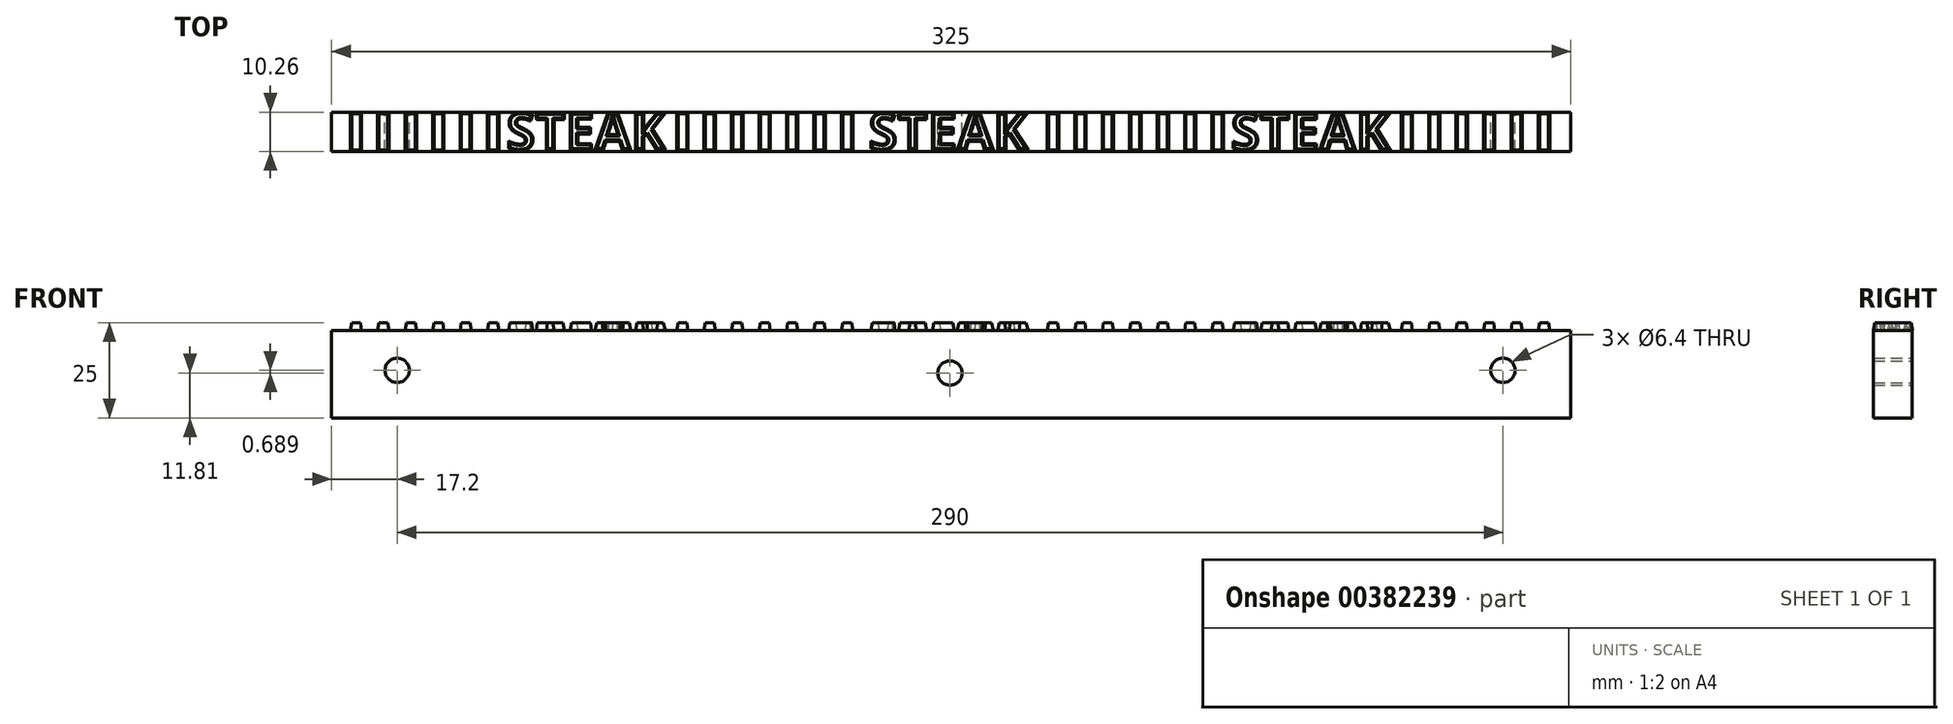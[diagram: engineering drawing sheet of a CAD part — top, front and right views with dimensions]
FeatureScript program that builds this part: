
annotation { "Feature Type Name" : "Feature", "Feature Type Description" : "" }
export const myFeature = defineFeature(function(context is Context, id is Id, definition is map)
    precondition{}
    {
        {
            var Q0;
            Q0=qCreatedBy(makeId("Front.planeOp"),FACE);
            var sketch = newSketch(context, id + "F0", { "sketchPlane" : qUnion([Q0])});
            skLineSegment(sketch, "E0.bottom", {"start": v(-162.2, 11.19) * mm, "end": v(162.8, 11.19) * mm});
            skLineSegment(sketch, "E0.top", {"start": v(-162.2, -11.81) * mm, "end": v(162.8, -11.81) * mm});
            skLineSegment(sketch, "E0.left", {"start": v(-162.2, 11.19) * mm, "end": v(-162.2, -11.81) * mm});
            skLineSegment(sketch, "E0.right", {"start": v(162.8, 11.19) * mm, "end": v(162.8, -11.81) * mm});
            skCircle(sketch, "E1", {"center": v(0, 0) * mm, "radius": 3.2 * mm});
            skCircle(sketch, "E2", {"center": v(145, 0.69) * mm, "radius": 3.2 * mm});
            skCircle(sketch, "E3", {"center": v(-145, 0.69) * mm, "radius": 3.2 * mm});
            skLineSegment(sketch, "E4", {"start": v(-154.88, 0.69) * mm, "end": v(156.24, 0.69) * mm});
            skSolve(sketch);
        }
        {
            var Q0;
            Q0 = qSketchRegion(id + "F0", true);
            extrude(context, id + "F1", {"entities" : qUnion([Q0]), "depth" : 10.2 * mm});
        }
        {
            var Q0;
            Q0=makeQuery(id+"F1.opExtrude","SWEPT_FACE",FACE,{"disambiguationData":[OSD([sQuery(id+"F0.wireOp",EDGE,"E0.bottom")])]});
            var sketch = newSketch(context, id + "F2", { "sketchPlane" : qUnion([Q0])});
            skLineSegment(sketch, "E5", {"start": v(0, 0) * mm, "end": v(0, -26.9) * mm, "construction": true});
            skLineSegment(sketch, "E6", {"start": v(-95, 0) * mm, "end": v(-95, -23.36) * mm, "construction": true});
            skLineSegment(sketch, "E7", {"start": v(95, 0) * mm, "end": v(95, -29.38) * mm, "construction": true});
            skSolve(sketch);
        }
        {
            var Q0;
            {var subQ0=sQuery(id+"F0.wireOp",EDGE,"E0.bottom");Q0=makeQuery(id+"F2.imprint","IMPRINT",FACE,{"disambiguationData":[TD([[makeQuery(id+"F2.imprint","IMPRINT",EDGE,{"derivedFrom":makeQuery(id+"F1.opExtrude","CAP_EDGE",EDGE,{"disambiguationData":[OSD([subQ0])],"isStart":true})}),-1.0]])]});}
            var sketch = newSketch(context, id + "F3", { "sketchPlane" : qUnion([Q0])});
            skText(sketch, "E8", { "text": "STEAK", "fontName": "OpenSans-Bold.ttf"});
            skText(sketch, "E9", { "text": "STEAK", "fontName": "OpenSans-Bold.ttf"});
            skText(sketch, "E10", { "text": "STEAK", "fontName": "OpenSans-Bold.ttf"});
            const initialGuessF3  = {"E8": [-0.1164, -0.0099, 1, 0, 0.0099], "E9": [-0.02137, -0.0099, 1, 0, 0.0099], "E10": [0.07366, -0.00994, 1, 0, 0.0099]};
            skSetInitialGuess(sketch, initialGuessF3);
            skSolve(sketch);
        }
        {
            var Q0;
            Q0 = qSketchRegion(id + "F3", true);
            extrude(context, id + "F4", {"entities" : qUnion([Q0]), "operationType" : NewBodyOperationType.ADD, "depth" : 2 * mm, "hasDraft" : true, "draftAngle" : 10 * degree, "draftPullDirection" : true});
        }
        {
            var Q0;
            {var subQ0=sQuery(id+"F0.wireOp",EDGE,"E0.bottom");Q0=makeQuery(id+"F2.imprint","IMPRINT",FACE,{"disambiguationData":[TD([[makeQuery(id+"F2.imprint","IMPRINT",EDGE,{"derivedFrom":makeQuery(id+"F1.opExtrude","CAP_EDGE",EDGE,{"disambiguationData":[OSD([subQ0])],"isStart":true})}),-1.0]])]});}
            var sketch = newSketch(context, id + "F5", { "sketchPlane" : qUnion([Q0])});
            skLineSegment(sketch, "E11", {"start": v(-45, 7.64) * mm, "end": v(-45, -24.35) * mm, "construction": true});
            skLineSegment(sketch, "E12", {"start": v(45, 7.5) * mm, "end": v(45, -24.35) * mm, "construction": true});
            skSolve(sketch);
        }
        {
            var Q0;
            {var subQ0=sQuery(id+"F0.wireOp",EDGE,"E0.bottom");Q0=makeQuery(id+"F2.imprint","IMPRINT",FACE,{"disambiguationData":[TD([[makeQuery(id+"F2.imprint","IMPRINT",EDGE,{"derivedFrom":makeQuery(id+"F1.opExtrude","CAP_EDGE",EDGE,{"disambiguationData":[OSD([subQ0])],"isStart":true})}),-1.0]])]});}
            var sketch = newSketch(context, id + "F6", { "sketchPlane" : qUnion([Q0])});
            skLineSegment(sketch, "E13.bottom", {"start": v(-47.1, 0) * mm, "end": v(-50.1, 0) * mm});
            skLineSegment(sketch, "E13.top", {"start": v(-47.1, -10.2) * mm, "end": v(-50.1, -10.2) * mm});
            skLineSegment(sketch, "E13.left", {"start": v(-47.1, 0) * mm, "end": v(-47.1, -10.2) * mm});
            skLineSegment(sketch, "E13.right", {"start": v(-50.1, 0) * mm, "end": v(-50.1, -10.2) * mm});
            skLineSegment(sketch, "E14.1.0.0", {"start": v(-54.3, 0) * mm, "end": v(-57.3, 0) * mm});
            skLineSegment(sketch, "E14.1.0.1", {"start": v(-54.3, 0) * mm, "end": v(-54.3, -10.2) * mm});
            skLineSegment(sketch, "E14.1.0.2", {"start": v(-57.3, 0) * mm, "end": v(-57.3, -10.2) * mm});
            skLineSegment(sketch, "E14.1.0.3", {"start": v(-54.3, -10.2) * mm, "end": v(-57.3, -10.2) * mm});
            skLineSegment(sketch, "E14.2.0.0", {"start": v(-61.5, 0) * mm, "end": v(-64.5, 0) * mm});
            skLineSegment(sketch, "E14.2.0.1", {"start": v(-61.5, 0) * mm, "end": v(-61.5, -10.2) * mm});
            skLineSegment(sketch, "E14.2.0.2", {"start": v(-64.5, 0) * mm, "end": v(-64.5, -10.2) * mm});
            skLineSegment(sketch, "E14.2.0.3", {"start": v(-61.5, -10.2) * mm, "end": v(-64.5, -10.2) * mm});
            skLineSegment(sketch, "E14.3.0.0", {"start": v(-68.7, 0) * mm, "end": v(-71.7, 0) * mm});
            skLineSegment(sketch, "E14.3.0.1", {"start": v(-68.7, 0) * mm, "end": v(-68.7, -10.2) * mm});
            skLineSegment(sketch, "E14.3.0.2", {"start": v(-71.7, 0) * mm, "end": v(-71.7, -10.2) * mm});
            skLineSegment(sketch, "E14.3.0.3", {"start": v(-68.7, -10.2) * mm, "end": v(-71.7, -10.2) * mm});
            skLineSegment(sketch, "E14.direction1", {"start": v(-50.1, 0) * mm, "end": v(-57.3, 0) * mm, "construction": true});
            skLineSegment(sketch, "E15.MirrorCS", {"start": v(-42.9, 0) * mm, "end": v(-42.9, -10.2) * mm});
            skLineSegment(sketch, "E16.MirrorCS", {"start": v(-39.9, 0) * mm, "end": v(-39.9, -10.2) * mm});
            skLineSegment(sketch, "E17.MirrorCS", {"start": v(-42.9, -10.2) * mm, "end": v(-39.9, -10.2) * mm});
            skLineSegment(sketch, "E18.MirrorCS", {"start": v(-42.9, 0) * mm, "end": v(-39.9, 0) * mm});
            skLineSegment(sketch, "E19.MirrorCS", {"start": v(-28.5, -10.2) * mm, "end": v(-25.5, -10.2) * mm});
            skLineSegment(sketch, "E20.MirrorCS", {"start": v(-35.7, 0) * mm, "end": v(-35.7, -10.2) * mm});
            skLineSegment(sketch, "E21.MirrorCS", {"start": v(-28.5, 0) * mm, "end": v(-28.5, -10.2) * mm});
            skLineSegment(sketch, "E22.MirrorCS", {"start": v(-35.7, 0) * mm, "end": v(-32.7, 0) * mm});
            skLineSegment(sketch, "E23.MirrorCS", {"start": v(-32.7, 0) * mm, "end": v(-32.7, -10.2) * mm});
            skLineSegment(sketch, "E24.MirrorCS", {"start": v(-28.5, 0) * mm, "end": v(-25.5, 0) * mm});
            skLineSegment(sketch, "E25.MirrorCS", {"start": v(-35.7, -10.2) * mm, "end": v(-32.7, -10.2) * mm});
            skLineSegment(sketch, "E26.MirrorCS", {"start": v(-25.5, 0) * mm, "end": v(-25.5, -10.2) * mm});
            skLineSegment(sketch, "E27.MirrorCS", {"start": v(42.9, -10.2) * mm, "end": v(39.9, -10.2) * mm});
            skLineSegment(sketch, "E28.MirrorCS", {"start": v(28.5, 0) * mm, "end": v(25.5, 0) * mm});
            skLineSegment(sketch, "E29.MirrorCS", {"start": v(68.7, 0) * mm, "end": v(68.7, -10.2) * mm});
            skLineSegment(sketch, "E30.MirrorCS", {"start": v(68.7, -10.2) * mm, "end": v(71.7, -10.2) * mm});
            skLineSegment(sketch, "E31.MirrorCS", {"start": v(47.1, 0) * mm, "end": v(50.1, 0) * mm});
            skLineSegment(sketch, "E32.MirrorCS", {"start": v(47.1, -10.2) * mm, "end": v(50.1, -10.2) * mm});
            skLineSegment(sketch, "E33.MirrorCS", {"start": v(35.7, 0) * mm, "end": v(32.7, 0) * mm});
            skLineSegment(sketch, "E34.MirrorCS", {"start": v(54.3, -10.2) * mm, "end": v(57.3, -10.2) * mm});
            skLineSegment(sketch, "E35.MirrorCS", {"start": v(68.7, 0) * mm, "end": v(71.7, 0) * mm});
            skLineSegment(sketch, "E36.MirrorCS", {"start": v(35.7, -10.2) * mm, "end": v(32.7, -10.2) * mm});
            skLineSegment(sketch, "E37.MirrorCS", {"start": v(50.1, 0) * mm, "end": v(57.3, 0) * mm, "construction": true});
            skLineSegment(sketch, "E38.MirrorCS", {"start": v(28.5, -10.2) * mm, "end": v(25.5, -10.2) * mm});
            skLineSegment(sketch, "E39.MirrorCS", {"start": v(61.5, -10.2) * mm, "end": v(64.5, -10.2) * mm});
            skLineSegment(sketch, "E40.MirrorCS", {"start": v(54.3, 0) * mm, "end": v(57.3, 0) * mm});
            skLineSegment(sketch, "E41.MirrorCS", {"start": v(61.5, 0) * mm, "end": v(64.5, 0) * mm});
            skLineSegment(sketch, "E42.MirrorCS", {"start": v(42.9, 0) * mm, "end": v(39.9, 0) * mm});
            skLineSegment(sketch, "E43.MirrorCS", {"start": v(25.5, 0) * mm, "end": v(25.5, -10.2) * mm});
            skLineSegment(sketch, "E44.MirrorCS", {"start": v(32.7, 0) * mm, "end": v(32.7, -10.2) * mm});
            skLineSegment(sketch, "E45.MirrorCS", {"start": v(71.7, 0) * mm, "end": v(71.7, -10.2) * mm});
            skLineSegment(sketch, "E46.MirrorCS", {"start": v(47.1, 0) * mm, "end": v(47.1, -10.2) * mm});
            skLineSegment(sketch, "E47.MirrorCS", {"start": v(57.3, 0) * mm, "end": v(57.3, -10.2) * mm});
            skLineSegment(sketch, "E48.MirrorCS", {"start": v(54.3, 0) * mm, "end": v(54.3, -10.2) * mm});
            skLineSegment(sketch, "E49.MirrorCS", {"start": v(50.1, 0) * mm, "end": v(50.1, -10.2) * mm});
            skLineSegment(sketch, "E50.MirrorCS", {"start": v(35.7, 0) * mm, "end": v(35.7, -10.2) * mm});
            skLineSegment(sketch, "E51.MirrorCS", {"start": v(64.5, 0) * mm, "end": v(64.5, -10.2) * mm});
            skLineSegment(sketch, "E52.MirrorCS", {"start": v(28.5, 0) * mm, "end": v(28.5, -10.2) * mm});
            skLineSegment(sketch, "E53.MirrorCS", {"start": v(39.9, 0) * mm, "end": v(39.9, -10.2) * mm});
            skLineSegment(sketch, "E54.MirrorCS", {"start": v(42.9, 0) * mm, "end": v(42.9, -10.2) * mm});
            skLineSegment(sketch, "E55.MirrorCS", {"start": v(61.5, 0) * mm, "end": v(61.5, -10.2) * mm});
            skLineSegment(sketch, "E56.MirrorCS", {"start": v(154.3, 0) * mm, "end": v(157.3, 0) * mm});
            skLineSegment(sketch, "E57.MirrorCS", {"start": v(147.1, 0) * mm, "end": v(150.1, 0) * mm});
            skLineSegment(sketch, "E58.MirrorCS", {"start": v(128.5, -10.2) * mm, "end": v(125.5, -10.2) * mm});
            skLineSegment(sketch, "E59.MirrorCS", {"start": v(142.9, -10.2) * mm, "end": v(139.9, -10.2) * mm});
            skLineSegment(sketch, "E60.MirrorCS", {"start": v(128.5, 0) * mm, "end": v(125.5, 0) * mm});
            skLineSegment(sketch, "E61.MirrorCS", {"start": v(121.3, -10.2) * mm, "end": v(118.3, -10.2) * mm});
            skLineSegment(sketch, "E62.MirrorCS", {"start": v(154.3, -10.2) * mm, "end": v(157.3, -10.2) * mm});
            skLineSegment(sketch, "E63.MirrorCS", {"start": v(142.9, 0) * mm, "end": v(139.9, 0) * mm});
            skLineSegment(sketch, "E64.MirrorCS", {"start": v(147.1, -10.2) * mm, "end": v(150.1, -10.2) * mm});
            skLineSegment(sketch, "E65.MirrorCS", {"start": v(135.7, 0) * mm, "end": v(132.7, 0) * mm});
            skLineSegment(sketch, "E66.MirrorCS", {"start": v(161.5, 0) * mm, "end": v(164.5, 0) * mm});
            skLineSegment(sketch, "E67.MirrorCS", {"start": v(121.3, 0) * mm, "end": v(121.3, -10.2) * mm});
            skLineSegment(sketch, "E68.MirrorCS", {"start": v(121.3, 0) * mm, "end": v(118.3, 0) * mm});
            skLineSegment(sketch, "E69.MirrorCS", {"start": v(161.5, -10.2) * mm, "end": v(164.5, -10.2) * mm});
            skLineSegment(sketch, "E70.MirrorCS", {"start": v(135.7, -10.2) * mm, "end": v(132.7, -10.2) * mm});
            skLineSegment(sketch, "E71.MirrorCS", {"start": v(135.7, 0) * mm, "end": v(135.7, -10.2) * mm});
            skLineSegment(sketch, "E72.MirrorCS", {"start": v(147.1, 0) * mm, "end": v(147.1, -10.2) * mm});
            skLineSegment(sketch, "E73.MirrorCS", {"start": v(132.7, 0) * mm, "end": v(132.7, -10.2) * mm});
            skLineSegment(sketch, "E74.MirrorCS", {"start": v(118.3, 0) * mm, "end": v(118.3, -10.2) * mm});
            skLineSegment(sketch, "E75.MirrorCS", {"start": v(125.5, 0) * mm, "end": v(125.5, -10.2) * mm});
            skLineSegment(sketch, "E76.MirrorCS", {"start": v(150.1, 0) * mm, "end": v(150.1, -10.2) * mm});
            skLineSegment(sketch, "E77.MirrorCS", {"start": v(139.9, 0) * mm, "end": v(132.7, 0) * mm, "construction": true});
            skLineSegment(sketch, "E78.MirrorCS", {"start": v(164.5, 0) * mm, "end": v(164.5, -10.2) * mm});
            skLineSegment(sketch, "E79.MirrorCS", {"start": v(157.3, 0) * mm, "end": v(157.3, -10.2) * mm});
            skLineSegment(sketch, "E80.MirrorCS", {"start": v(142.9, 0) * mm, "end": v(142.9, -10.2) * mm});
            skLineSegment(sketch, "E81.MirrorCS", {"start": v(154.3, 0) * mm, "end": v(154.3, -10.2) * mm});
            skLineSegment(sketch, "E82.MirrorCS", {"start": v(161.5, 0) * mm, "end": v(161.5, -10.2) * mm});
            skLineSegment(sketch, "E83.MirrorCS", {"start": v(128.5, 0) * mm, "end": v(128.5, -10.2) * mm});
            skLineSegment(sketch, "E84.MirrorCS", {"start": v(139.9, 0) * mm, "end": v(139.9, -10.2) * mm});
            skLineSegment(sketch, "E85.MirrorCS", {"start": v(-121.3, 0) * mm, "end": v(-121.3, -10.2) * mm});
            skLineSegment(sketch, "E86.MirrorCS", {"start": v(-135.7, 0) * mm, "end": v(-132.7, 0) * mm});
            skLineSegment(sketch, "E87.MirrorCS", {"start": v(-135.7, -10.2) * mm, "end": v(-132.7, -10.2) * mm});
            skLineSegment(sketch, "E88.MirrorCS", {"start": v(-132.7, 0) * mm, "end": v(-132.7, -10.2) * mm});
            skLineSegment(sketch, "E89.MirrorCS", {"start": v(-135.7, 0) * mm, "end": v(-135.7, -10.2) * mm});
            skLineSegment(sketch, "E90.MirrorCS", {"start": v(-139.9, 0) * mm, "end": v(-132.7, 0) * mm, "construction": true});
            skLineSegment(sketch, "E91.MirrorCS", {"start": v(-142.9, 0) * mm, "end": v(-142.9, -10.2) * mm});
            skLineSegment(sketch, "E92.MirrorCS", {"start": v(-147.1, 0) * mm, "end": v(-150.1, 0) * mm});
            skLineSegment(sketch, "E93.MirrorCS", {"start": v(-142.9, -10.2) * mm, "end": v(-139.9, -10.2) * mm});
            skLineSegment(sketch, "E94.MirrorCS", {"start": v(-142.9, 0) * mm, "end": v(-139.9, 0) * mm});
            skLineSegment(sketch, "E95.MirrorCS", {"start": v(-139.9, 0) * mm, "end": v(-139.9, -10.2) * mm});
            skLineSegment(sketch, "E96.MirrorCS", {"start": v(-161.5, -10.2) * mm, "end": v(-164.5, -10.2) * mm});
            skLineSegment(sketch, "E97.MirrorCS", {"start": v(-154.3, -10.2) * mm, "end": v(-157.3, -10.2) * mm});
            skLineSegment(sketch, "E98.MirrorCS", {"start": v(-121.3, 0) * mm, "end": v(-118.3, 0) * mm});
            skLineSegment(sketch, "E99.MirrorCS", {"start": v(-128.5, -10.2) * mm, "end": v(-125.5, -10.2) * mm});
            skLineSegment(sketch, "E100.MirrorCS", {"start": v(-125.5, 0) * mm, "end": v(-125.5, -10.2) * mm});
            skLineSegment(sketch, "E101.MirrorCS", {"start": v(-128.5, 0) * mm, "end": v(-128.5, -10.2) * mm});
            skLineSegment(sketch, "E102.MirrorCS", {"start": v(-128.5, 0) * mm, "end": v(-125.5, 0) * mm});
            skLineSegment(sketch, "E103.MirrorCS", {"start": v(-164.5, 0) * mm, "end": v(-164.5, -10.2) * mm});
            skLineSegment(sketch, "E104.MirrorCS", {"start": v(-154.3, 0) * mm, "end": v(-154.3, -10.2) * mm});
            skLineSegment(sketch, "E105.MirrorCS", {"start": v(-161.5, 0) * mm, "end": v(-161.5, -10.2) * mm});
            skLineSegment(sketch, "E106.MirrorCS", {"start": v(-154.3, 0) * mm, "end": v(-157.3, 0) * mm});
            skLineSegment(sketch, "E107.MirrorCS", {"start": v(-147.1, 0) * mm, "end": v(-147.1, -10.2) * mm});
            skLineSegment(sketch, "E108.MirrorCS", {"start": v(-157.3, 0) * mm, "end": v(-157.3, -10.2) * mm});
            skLineSegment(sketch, "E109.MirrorCS", {"start": v(-118.3, 0) * mm, "end": v(-118.3, -10.2) * mm});
            skLineSegment(sketch, "E110.MirrorCS", {"start": v(-147.1, -10.2) * mm, "end": v(-150.1, -10.2) * mm});
            skLineSegment(sketch, "E111.MirrorCS", {"start": v(-161.5, 0) * mm, "end": v(-164.5, 0) * mm});
            skLineSegment(sketch, "E112.MirrorCS", {"start": v(-121.3, -10.2) * mm, "end": v(-118.3, -10.2) * mm});
            skLineSegment(sketch, "E113.MirrorCS", {"start": v(-150.1, 0) * mm, "end": v(-150.1, -10.2) * mm});
            skSolve(sketch);
        }
        {
            var Q0;
            Q0=makeQuery(id+"F6.imprint","IMPRINT",FACE,{"disambiguationData":[TD([[makeQuery(id+"F6.imprint","IMPRINT",EDGE,{"derivedFrom":sQuery(id+"F6.wireOp",EDGE,"E13.bottom")}),-1.0]])]});
            var Q1;
            Q1=makeQuery(id+"F6.imprint","IMPRINT",FACE,{"disambiguationData":[TD([[makeQuery(id+"F6.imprint","IMPRINT",EDGE,{"derivedFrom":sQuery(id+"F6.wireOp",EDGE,"E14.1.0.0")}),-1.0]])]});
            var Q2;
            Q2=makeQuery(id+"F6.imprint","IMPRINT",FACE,{"disambiguationData":[TD([[makeQuery(id+"F6.imprint","IMPRINT",EDGE,{"derivedFrom":sQuery(id+"F6.wireOp",EDGE,"E14.2.0.0")}),-1.0]])]});
            var Q3;
            Q3=makeQuery(id+"F6.imprint","IMPRINT",FACE,{"disambiguationData":[TD([[makeQuery(id+"F6.imprint","IMPRINT",EDGE,{"derivedFrom":sQuery(id+"F6.wireOp",EDGE,"E14.3.0.0")}),-1.0]])]});
            var Q4;
            Q4=makeQuery(id+"F6.imprint","IMPRINT",FACE,{"disambiguationData":[TD([[makeQuery(id+"F6.imprint","IMPRINT",EDGE,{"derivedFrom":sQuery(id+"F6.wireOp",EDGE,"E15.MirrorCS")}),1.0]])]});
            var Q5;
            Q5=makeQuery(id+"F6.imprint","IMPRINT",FACE,{"disambiguationData":[TD([[makeQuery(id+"F6.imprint","IMPRINT",EDGE,{"derivedFrom":sQuery(id+"F6.wireOp",EDGE,"E20.MirrorCS")}),1.0]])]});
            var Q6;
            Q6=makeQuery(id+"F6.imprint","IMPRINT",FACE,{"disambiguationData":[TD([[makeQuery(id+"F6.imprint","IMPRINT",EDGE,{"derivedFrom":sQuery(id+"F6.wireOp",EDGE,"E27.MirrorCS")}),1.0]])]});
            var Q7;
            Q7=makeQuery(id+"F6.imprint","IMPRINT",FACE,{"disambiguationData":[TD([[makeQuery(id+"F6.imprint","IMPRINT",EDGE,{"derivedFrom":sQuery(id+"F6.wireOp",EDGE,"E28.MirrorCS")}),-1.0]])]});
            var Q8;
            Q8=makeQuery(id+"F6.imprint","IMPRINT",FACE,{"disambiguationData":[TD([[makeQuery(id+"F6.imprint","IMPRINT",EDGE,{"derivedFrom":sQuery(id+"F6.wireOp",EDGE,"E30.MirrorCS")}),1.0]])]});
            var Q9;
            Q9=makeQuery(id+"F6.imprint","IMPRINT",FACE,{"disambiguationData":[TD([[makeQuery(id+"F6.imprint","IMPRINT",EDGE,{"derivedFrom":sQuery(id+"F6.wireOp",EDGE,"E31.MirrorCS")}),-1.0]])]});
            var Q10;
            Q10=makeQuery(id+"F6.imprint","IMPRINT",FACE,{"disambiguationData":[TD([[makeQuery(id+"F6.imprint","IMPRINT",EDGE,{"derivedFrom":sQuery(id+"F6.wireOp",EDGE,"E33.MirrorCS")}),-1.0]])]});
            var Q11;
            Q11=makeQuery(id+"F6.imprint","IMPRINT",FACE,{"disambiguationData":[TD([[makeQuery(id+"F6.imprint","IMPRINT",EDGE,{"derivedFrom":sQuery(id+"F6.wireOp",EDGE,"E34.MirrorCS")}),1.0]])]});
            var Q12;
            Q12=makeQuery(id+"F6.imprint","IMPRINT",FACE,{"disambiguationData":[TD([[makeQuery(id+"F6.imprint","IMPRINT",EDGE,{"derivedFrom":sQuery(id+"F6.wireOp",EDGE,"E39.MirrorCS")}),1.0]])]});
            var Q13;
            Q13=makeQuery(id+"F6.imprint","IMPRINT",FACE,{"disambiguationData":[TD([[makeQuery(id+"F6.imprint","IMPRINT",EDGE,{"derivedFrom":sQuery(id+"F6.wireOp",EDGE,"E56.MirrorCS")}),-1.0]])]});
            var Q14;
            Q14=makeQuery(id+"F6.imprint","IMPRINT",FACE,{"disambiguationData":[TD([[makeQuery(id+"F6.imprint","IMPRINT",EDGE,{"derivedFrom":sQuery(id+"F6.wireOp",EDGE,"E57.MirrorCS")}),-1.0]])]});
            var Q15;
            Q15=makeQuery(id+"F6.imprint","IMPRINT",FACE,{"disambiguationData":[TD([[makeQuery(id+"F6.imprint","IMPRINT",EDGE,{"derivedFrom":sQuery(id+"F6.wireOp",EDGE,"E58.MirrorCS")}),1.0]])]});
            var Q16;
            Q16=makeQuery(id+"F6.imprint","IMPRINT",FACE,{"disambiguationData":[TD([[makeQuery(id+"F6.imprint","IMPRINT",EDGE,{"derivedFrom":sQuery(id+"F6.wireOp",EDGE,"E59.MirrorCS")}),1.0]])]});
            var Q17;
            Q17=makeQuery(id+"F6.imprint","IMPRINT",FACE,{"disambiguationData":[TD([[makeQuery(id+"F6.imprint","IMPRINT",EDGE,{"derivedFrom":sQuery(id+"F6.wireOp",EDGE,"E61.MirrorCS")}),1.0]])]});
            var Q18;
            Q18=makeQuery(id+"F6.imprint","IMPRINT",FACE,{"disambiguationData":[TD([[makeQuery(id+"F6.imprint","IMPRINT",EDGE,{"derivedFrom":sQuery(id+"F6.wireOp",EDGE,"E65.MirrorCS")}),-1.0]])]});
            var Q19;
            Q19=makeQuery(id+"F6.imprint","IMPRINT",FACE,{"disambiguationData":[TD([[makeQuery(id+"F6.imprint","IMPRINT",EDGE,{"derivedFrom":sQuery(id+"F6.wireOp",EDGE,"E86.MirrorCS")}),-1.0]])]});
            var Q20;
            Q20=makeQuery(id+"F6.imprint","IMPRINT",FACE,{"disambiguationData":[TD([[makeQuery(id+"F6.imprint","IMPRINT",EDGE,{"derivedFrom":sQuery(id+"F6.wireOp",EDGE,"E91.MirrorCS")}),1.0]])]});
            var Q21;
            Q21=makeQuery(id+"F6.imprint","IMPRINT",FACE,{"disambiguationData":[TD([[makeQuery(id+"F6.imprint","IMPRINT",EDGE,{"derivedFrom":sQuery(id+"F6.wireOp",EDGE,"E92.MirrorCS")}),-1.0]])]});
            var Q22;
            Q22=makeQuery(id+"F6.imprint","IMPRINT",FACE,{"disambiguationData":[TD([[makeQuery(id+"F6.imprint","IMPRINT",EDGE,{"derivedFrom":sQuery(id+"F6.wireOp",EDGE,"E85.MirrorCS")}),1.0]])]});
            var Q23;
            Q23=makeQuery(id+"F6.imprint","IMPRINT",FACE,{"disambiguationData":[TD([[makeQuery(id+"F6.imprint","IMPRINT",EDGE,{"derivedFrom":sQuery(id+"F6.wireOp",EDGE,"E97.MirrorCS")}),1.0]])]});
            var Q24;
            Q24=makeQuery(id+"F6.imprint","IMPRINT",FACE,{"disambiguationData":[TD([[makeQuery(id+"F6.imprint","IMPRINT",EDGE,{"derivedFrom":sQuery(id+"F6.wireOp",EDGE,"E99.MirrorCS")}),1.0]])]});
            var Q25;
            Q25=makeQuery(id+"F6.imprint","IMPRINT",FACE,{"disambiguationData":[TD([[makeQuery(id+"F6.imprint","IMPRINT",EDGE,{"derivedFrom":sQuery(id+"F6.wireOp",EDGE,"E24.MirrorCS")}),-1.0]])]});
            extrude(context, id + "F7", {"entities" : qUnion([Q0, Q1, Q2, Q3, Q4, Q5, Q6, Q7, Q8, Q9, Q10, Q11, Q12, Q13, Q14, Q15, Q16, Q17, Q18, Q19, Q20, Q21, Q22, Q23, Q24, Q25]), "operationType" : NewBodyOperationType.ADD, "depth" : 2 * mm, "hasDraft" : true, "draftAngle" : 10 * degree, "draftPullDirection" : true});
        }
    });
